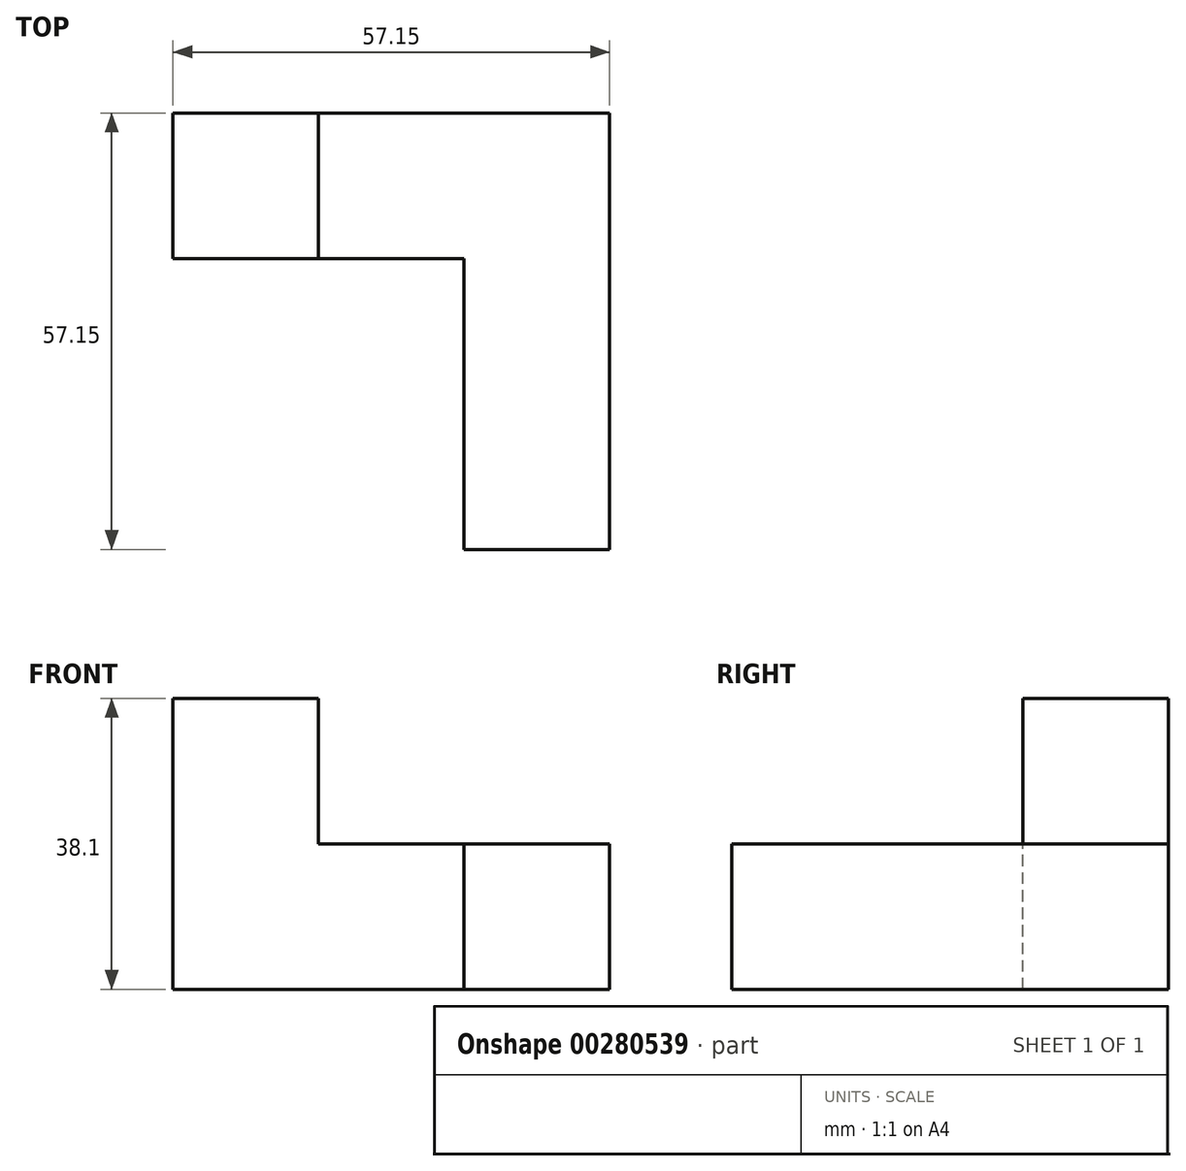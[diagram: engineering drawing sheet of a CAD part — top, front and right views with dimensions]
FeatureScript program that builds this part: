
annotation { "Feature Type Name" : "Feature", "Feature Type Description" : "" }
export const myFeature = defineFeature(function(context is Context, id is Id, definition is map)
    precondition{}
    {
        {
            var Q0;
            Q0=qCreatedBy(makeId("Top.planeOp"),FACE);
            var sketch = newSketch(context, id + "F0", { "sketchPlane" : qUnion([Q0])});
            skLineSegment(sketch, "E0.bottom", {"start": v(0, 0) * mm, "end": v(19.05, 0) * mm});
            skLineSegment(sketch, "E0.top", {"start": v(0, 57.15) * mm, "end": v(19.05, 57.15) * mm});
            skLineSegment(sketch, "E0.left", {"start": v(0, 0) * mm, "end": v(0, 57.15) * mm});
            skLineSegment(sketch, "E0.right", {"start": v(19.05, 0) * mm, "end": v(19.05, 57.15) * mm});
            skSolve(sketch);
        }
        {
            var Q0;
            Q0 = qSketchRegion(id + "F0", true);
            extrude(context, id + "F1", {"entities" : qUnion([Q0]), "depth" : 19.05 * mm});
        }
        {
            var Q0;
            Q0=makeQuery(id+"F1.opExtrude","SWEPT_FACE",FACE,{"disambiguationData":[OSD([sQuery(id+"F0.wireOp",EDGE,"E0.left")])]});
            var sketch = newSketch(context, id + "F2", { "sketchPlane" : qUnion([Q0])});
            skLineSegment(sketch, "E1.bottom", {"start": v(-57.15, 0) * mm, "end": v(-38.1, 0) * mm});
            skLineSegment(sketch, "E1.top", {"start": v(-57.15, 19.05) * mm, "end": v(-38.1, 19.05) * mm});
            skLineSegment(sketch, "E1.left", {"start": v(-57.15, 0) * mm, "end": v(-57.15, 19.05) * mm});
            skLineSegment(sketch, "E1.right", {"start": v(-38.1, 0) * mm, "end": v(-38.1, 19.05) * mm});
            skSolve(sketch);
        }
        {
            var Q0;
            Q0 = qSketchRegion(id + "F2", true);
            extrude(context, id + "F3", {"entities" : qUnion([Q0]), "operationType" : NewBodyOperationType.ADD, "depth" : 38.1 * mm});
        }
        {
            var Q0;
            Q0=makeQuery(id+"F3.boolean.opBoolean","MERGE",FACE,{"derivedFrom":[makeQuery(id+"F1.opExtrude","CAP_FACE",FACE,{"disambiguationData":[OSD([sQuery(id+"F0.wireOp",EDGE,"E0.bottom"),sQuery(id+"F0.wireOp",EDGE,"E0.top"),sQuery(id+"F0.wireOp",EDGE,"E0.left"),sQuery(id+"F0.wireOp",EDGE,"E0.right")])],"isStart":false}),makeQuery(id+"F3.opExtrude","SWEPT_FACE",FACE,{"disambiguationData":[OSD([sQuery(id+"F2.wireOp",EDGE,"E1.top")])]})]});
            var sketch = newSketch(context, id + "F4", { "sketchPlane" : qUnion([Q0])});
            skLineSegment(sketch, "E2.bottom", {"start": v(-38.1, 38.1) * mm, "end": v(-19.05, 38.1) * mm});
            skLineSegment(sketch, "E2.top", {"start": v(-38.1, 57.15) * mm, "end": v(-19.05, 57.15) * mm});
            skLineSegment(sketch, "E2.left", {"start": v(-38.1, 38.1) * mm, "end": v(-38.1, 57.15) * mm});
            skLineSegment(sketch, "E2.right", {"start": v(-19.05, 38.1) * mm, "end": v(-19.05, 57.15) * mm});
            skSolve(sketch);
        }
        {
            var Q0;
            Q0 = qSketchRegion(id + "F4", true);
            extrude(context, id + "F5", {"entities" : qUnion([Q0]), "operationType" : NewBodyOperationType.ADD, "depth" : 19.05 * mm});
        }
    });
